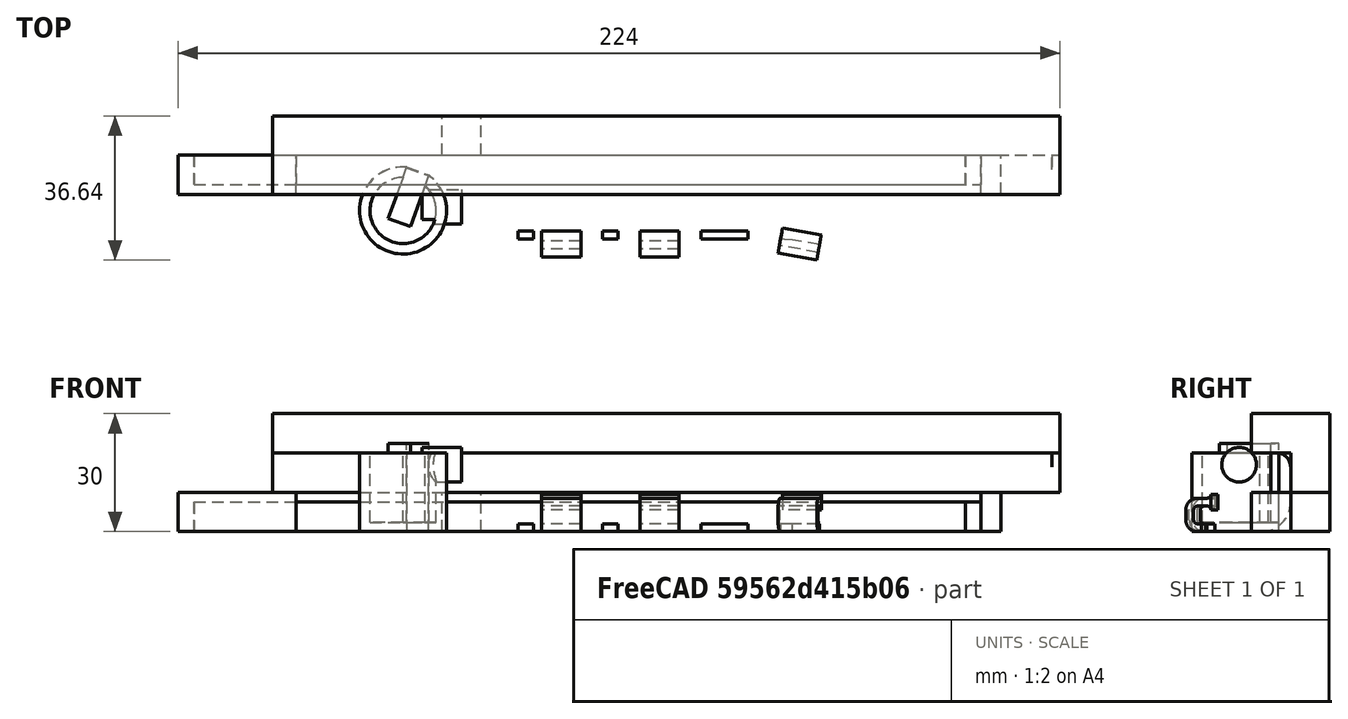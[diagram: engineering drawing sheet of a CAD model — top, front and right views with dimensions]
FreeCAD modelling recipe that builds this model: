
FCSTD DOCUMENT  (FreeCAD 0.19R0.19.2)
Label: v0_71
License: All rights reserved
LicenseURL: http://en.wikipedia.org/wiki/All_rights_reserved
objects: Part::Box×62, Part::Fillet×31, Part::MultiFuse×26, Part::Cut×14, Sketcher::SketchObject×10, Part::Extrusion×9, Part::Cylinder×6, App::MeasureDistance×3, Part::Revolution×1
note: 159 computed .brp shape members not serialized (recipe doc carries the construction recipe); baked Part::Feature solids carry a one-line shape summary decoded from their .brp

FEATURE [Sketcher::SketchObject] Sketch001
  FullyConstrained = true
  sketch-geometry (47):
    g0: Circle CenterX=-129.5 CenterY=-8 CenterZ=0 NormalX=0 NormalY=0 NormalZ=1 AngleXU=0 Radius=1
    g1: Circle CenterX=-129.5 CenterY=-3 CenterZ=0 NormalX=0 NormalY=0 NormalZ=1 AngleXU=0 Radius=1
    g2: Circle CenterX=-124.5 CenterY=-3 CenterZ=0 NormalX=0 NormalY=0 NormalZ=1 AngleXU=0 Radius=1
    g3: BSplineCurve PolesCount=3 KnotsCount=2 Degree=2 IsPeriodic=0
    g4: GeomPoint X=-129.5 Y=-8 Z=0
    g5: GeomPoint X=-124.5 Y=-3 Z=0
    g6: LineSegment StartX=18.6 StartY=-2.9 StartZ=0 EndX=23.6 EndY=-2.9 EndZ=0
    g7: ArcOfCircle CenterX=23.8 CenterY=-14.35 CenterZ=0 NormalX=0 NormalY=0 NormalZ=1 AngleXU=0 Radius=2.3 StartAngle=8e-16 EndAngle=1.5708
    g8: ArcOfCircle CenterX=23.8 CenterY=-18.1 CenterZ=0 NormalX=0 NormalY=0 NormalZ=1 AngleXU=0 Radius=2.3 StartAngle=4.71239 EndAngle=6.28319
    g9: LineSegment StartX=23.8 StartY=-20.4 StartZ=0 EndX=21.1 EndY=-20.4 EndZ=0
    g10: LineSegment StartX=21.1 StartY=-22.9 StartZ=0 EndX=21.1 EndY=-20.4 EndZ=0
    g11: LineSegment StartX=26.1 StartY=-14.35 StartZ=0 EndX=26.1 EndY=-18.1 EndZ=0
    g12: LineSegment StartX=18.6 StartY=-5.40742 StartZ=0 EndX=18.6 EndY=-2.9 EndZ=0
    g13: ArcOfCircle CenterX=18.8 CenterY=-8.1 CenterZ=0 NormalX=0 NormalY=0 NormalZ=1 AngleXU=0 Radius=2.7 StartAngle=1.64494 EndAngle=3.14159
    g14: ArcOfCircle CenterX=18.8 CenterY=-11.85 CenterZ=0 NormalX=0 NormalY=0 NormalZ=1 AngleXU=0 Radius=2.7 StartAngle=3.14159 EndAngle=4.71239
    g15: LineSegment StartX=16.1 StartY=-8.1 StartZ=0 EndX=16.1 EndY=-11.85 EndZ=0
    g16: LineSegment StartX=18.8 StartY=-14.55 StartZ=0 EndX=21.5 EndY=-14.55 EndZ=0
    g17: LineSegment StartX=21.5 StartY=-12.05 StartZ=0 EndX=21.5 EndY=-14.55 EndZ=0
    g18: LineSegment StartX=21.5 StartY=-12.05 StartZ=0 EndX=23.8 EndY=-12.05 EndZ=0
    g19: LineSegment StartX=16.1 StartY=-22.9 StartZ=0 EndX=21.1 EndY=-22.9 EndZ=0
    g20: LineSegment StartX=23.6 StartY=-2.9 StartZ=0 EndX=23.6 EndY=0 EndZ=0
    g21: LineSegment StartX=16.1 StartY=-22.9 StartZ=0 EndX=16.1 EndY=-26.2 EndZ=0
    g22: BSplineCurve PolesCount=3 KnotsCount=2 Degree=2 IsPeriodic=0
    g23: LineSegment StartX=2.6 StartY=-3 StartZ=0 EndX=-124.5 EndY=-3 EndZ=0
    g24: ArcOfCircle CenterX=-134.9 CenterY=-8.6 CenterZ=0 NormalX=0 NormalY=0 NormalZ=1 AngleXU=0 Radius=0.5 StartAngle=4.71238 EndAngle=6.28319
    g25: LineSegment StartX=-141.9 StartY=-9.1 StartZ=0 EndX=-134.9 EndY=-9.1 EndZ=0
    g26: LineSegment StartX=-141.9 StartY=-33.8 StartZ=0 EndX=-141.5 EndY=-33.8 EndZ=0
    g27: LineSegment StartX=-141.9 StartY=-9.1 StartZ=0 EndX=-141.9 EndY=-33.8 EndZ=0
    g28: LineSegment StartX=-134.4 StartY=-8.6 StartZ=0 EndX=-134.4 EndY=0 EndZ=0
    g29: LineSegment StartX=-134.4 StartY=0 StartZ=0 EndX=23.6 EndY=0 EndZ=0
    g30: LineSegment StartX=-133.5 StartY=-26.2 StartZ=0 EndX=16.1 EndY=-26.2 EndZ=0
    g31-g36: Circle x6 (B-spline internal-alignment scaffolding for g37; pole/knot coordinates omitted)
    g37: BSplineCurve PolesCount=6 KnotsCount=4 Degree=3 IsPeriodic=0
    g38-g41: GeomPoint x4 (B-spline internal-alignment scaffolding for g37; pole/knot coordinates omitted)
    g42: BSplineCurve PolesCount=3 KnotsCount=2 Degree=2 IsPeriodic=0
    g43: LineSegment StartX=-129.5 StartY=-8 StartZ=0 EndX=-129.5 EndY=-18.2 EndZ=0
    g44: BSplineCurve PolesCount=3 KnotsCount=2 Degree=2 IsPeriodic=0
    g45: LineSegment StartX=7.6 StartY=-8 StartZ=0 EndX=7.6 EndY=-18.2 EndZ=0
    g46: LineSegment StartX=2.6 StartY=-23.2 StartZ=0 EndX=-124.5 EndY=-23.2 EndZ=0
  constraints (87):
    c: Weight(g0) = 1
    c: Equal(g0,g1)
    c: Equal(g0,g2)
    c: InternalAlignment(g0,g3)
    c: InternalAlignment(g1,g3)
    c: InternalAlignment(g2,g3)
    c: InternalAlignment(g4,g3)
    c: InternalAlignment(g5,g3)
    c: Block(g3)
    c: Block(g8)
    c: Block(g7)
    c: Coincident(g9,g8)
    c: Horizontal(g9)
    c: Vertical(g10)
    c: Coincident(g10,g9)
    c: Coincident(g11,g7)
    c: Coincident(g11,g8)
    c: Vertical(g11)
    c: Vertical(g12)
    c: Block(g12)
    c: Coincident(g6,g12)
    c: Horizontal(g6)
    c: Block(g6)
    c: Coincident(g13,g12)
    c: Block(g14)
    c: Vertical(g15)
    c: Block(g15)
    c: Coincident(g16,g14)
    c: Horizontal(g16)
    c: Vertical(g17)
    c: Coincident(g17,g16)
    c: Block(g17)
    c: Coincident(g18,g7)
    c: Horizontal(g18)
    c: Block(g18)
    c: Coincident(g19,g10)
    c: Horizontal(g19)
    c: Block(g19)
    c: Block(g13)
    c: Coincident(g20,g6)
    c: Vertical(g20)
    c: Vertical(g21)
    c: Block(g21)
    c: Block(g22)
    c: Coincident(g23,g22)
    c: Coincident(g23,g3)
    c: Horizontal(g23)
    c: Block(g24)
    c: Coincident(g25,g24)
    c: Horizontal(g25)
    c: Horizontal(g26)
    c: Block(g26)
    c: Coincident(g27,g25)
    c: Coincident(g27,g26)
    c: Vertical(g27)
    c: Coincident(g28,g24)
    c: Vertical(g28)
    c: Coincident(g29,g28)
    c: Coincident(g29,g20)
    c: Horizontal(g29)
    c: Block(g29)
    c: Block(g25)
    c: Block(g28)
    c: Block(g27)
    c: Coincident(g30,g21)
    c: Horizontal(g30)
    c: Block(g30)
    c: Coincident(g37,g26)
    c: Weight(g31) = 1
    c: Equal(g31, g32-g36) x5
    c: Coincident(g37,g30)
    c: InternalAlignment(g31-g36 -> g37) x6
    c: InternalAlignment(g38-g41 -> g37) x4
    c: Block(g37)
    c: Block(g42)
    c: Coincident(g43,g3)
    c: Coincident(g43,g42)
    c: Vertical(g43)
    c: Distance(g43) = 10.2
    c: Block(g44)
    c: Coincident(g45,g22)
    c: Coincident(g45,g44)
    c: Vertical(g45)
    c: Distance(g45) = 10.2
    c: Coincident(g46,g44)
    c: Coincident(g46,g42)
    c: Horizontal(g46)
FEATURE [Part::Extrusion] Extrude001
  Base = -> Sketch001
  Dir = (0,0,1)
  DirMode = 2
  FaceMakerClass = Part::FaceMakerBullseye
  LengthFwd = 20
  LengthRev = 0
  Solid = true
  Symmetric = false
FEATURE [Sketcher::SketchObject] Sketch004
  FullyConstrained = true
  Placement = pos=(0,0,0) rot=(1,0,0;1.5708rad)
  sketch-geometry (12):
    g0: LineSegment StartX=15.75 StartY=2.5 StartZ=0 EndX=15.75 EndY=0 EndZ=0
    g1: Circle CenterX=15.75 CenterY=2.5 CenterZ=0 NormalX=0 NormalY=0 NormalZ=1 AngleXU=0 Radius=1
    g2: Circle CenterX=10.55 CenterY=2.5 CenterZ=0 NormalX=0 NormalY=0 NormalZ=1 AngleXU=0 Radius=1
    g3: Circle CenterX=10.55 CenterY=8 CenterZ=0 NormalX=0 NormalY=0 NormalZ=1 AngleXU=0 Radius=1
    g4: BSplineCurve PolesCount=3 KnotsCount=2 Degree=2 IsPeriodic=0
    g5: GeomPoint X=15.75 Y=2.5 Z=0
    g6: GeomPoint X=10.55 Y=8 Z=0
    g7: LineSegment StartX=1.9 StartY=8 StartZ=0 EndX=10.55 EndY=8 EndZ=0
    g8: LineSegment StartX=1.9 StartY=-2.4 StartZ=0 EndX=1.9 EndY=8 EndZ=0
    g9: LineSegment StartX=3.30092 StartY=-2.4 StartZ=0 EndX=3.30092 EndY=0 EndZ=0
    g10: LineSegment StartX=15.75 StartY=0 StartZ=0 EndX=3.30092 EndY=0 EndZ=0
    g11: LineSegment StartX=3.30092 StartY=-2.4 StartZ=0 EndX=1.9 EndY=-2.4 EndZ=0
  constraints (26):
    c: Vertical(g0)
    c: Distance(g0) = 2.5
    c: Coincident(g4,g0)
    c: Weight(g1) = 1
    c: Equal(g1,g2)
    c: Equal(g1,g3)
    c: InternalAlignment(g1,g4)
    c: InternalAlignment(g2,g4)
    c: InternalAlignment(g3,g4)
    c: InternalAlignment(g5,g4)
    c: InternalAlignment(g6,g4)
    c: Block(g4)
    c: Coincident(g7,g4)
    c: Horizontal(g7)
    c: Vertical(g8)
    c: Coincident(g8,g7)
    c: Block(g8)
    c: Vertical(g9)
    c: Coincident(g10,g0)
    c: PointOnObject(g10,g-1)
    c: Horizontal(g10)
    c: Coincident(g10,g9)
    c: Block(g9)
    c: Coincident(g11,g9)
    c: Coincident(g11,g8)
    c: Horizontal(g11)
FEATURE [Part::Revolution] Revolve  label="mainScrewStandRevolve"
  Angle = 360
  Axis = (0,0,1)
  Base = (0,0,0)
  FaceMakerClass = Part::FaceMakerBullseye
  Placement = pos=(-101.95,-15.3,0) rot=(0,0,1;0rad)
  Solid = true
  Source = -> Sketch004
  Symmetric = false
FEATURE [Sketcher::SketchObject] Sketch044
  FullyConstrained = true
  MapMode = 4
  Placement = pos=(0,0,0) rot=(0.57735,0.57735,0.57735;2.0944rad)
  sketch-geometry (14):
    g0: LineSegment StartX=6.08745 StartY=-4.11588 StartZ=0 EndX=6.08745 EndY=-2.11589 EndZ=0
    g1: LineSegment StartX=8.08745 StartY=1.38411 StartZ=0 EndX=8.08745 EndY=-1.11589 EndZ=0
    g2: ArcOfCircle CenterX=7.08745 CenterY=-1.11589 CenterZ=0 NormalX=0 NormalY=0 NormalZ=1 AngleXU=0 Radius=1 StartAngle=4.71239 EndAngle=6.28319
    g3: LineSegment StartX=6.08745 StartY=-2.11589 StartZ=0 EndX=7.08745 EndY=-2.11589 EndZ=0
    g4: LineSegment StartX=6.08745 StartY=-4.11588 StartZ=0 EndX=7.08745 EndY=-4.11588 EndZ=0
    g5: ArcOfCircle CenterX=7.08745 CenterY=-1.11589 CenterZ=0 NormalX=0 NormalY=0 NormalZ=1 AngleXU=0 Radius=3 StartAngle=4.71239 EndAngle=6.28319
    g6: ArcOfCircle CenterX=7.08745 CenterY=1.38411 CenterZ=0 NormalX=0 NormalY=0 NormalZ=1 AngleXU=0 Radius=1 StartAngle=5.35e-14 EndAngle=1.5708
    g7: LineSegment StartX=10.0875 StartY=-1.11588 StartZ=0 EndX=10.0875 EndY=1.38411 EndZ=0
    g8: ArcOfCircle CenterX=7.08745 CenterY=1.38411 CenterZ=0 NormalX=0 NormalY=0 NormalZ=1 AngleXU=0 Radius=3 StartAngle=3.57e-14 EndAngle=1.5708
    g9: ArcOfCircle CenterX=4.58745 CenterY=1.38412 CenterZ=0 NormalX=0 NormalY=0 NormalZ=1 AngleXU=0 Radius=1 StartAngle=1.57081 EndAngle=3.14159
    g10: LineSegment StartX=4.58744 StartY=2.38411 StartZ=0 EndX=7.08745 EndY=2.38411 EndZ=0
    g11: LineSegment StartX=4.58745 StartY=4.38411 StartZ=0 EndX=7.08745 EndY=4.38411 EndZ=0
    g12: ArcOfCircle CenterX=4.58745 CenterY=5.38411 CenterZ=0 NormalX=0 NormalY=0 NormalZ=1 AngleXU=0 Radius=1 StartAngle=3.14159 EndAngle=4.71239
    g13: LineSegment StartX=3.58745 StartY=5.38411 StartZ=0 EndX=3.58745 EndY=1.38411 EndZ=0
  constraints (33):
    c: Vertical(g0)
    c: Block(g0)
    c: Block(g1)
    c: Coincident(g2,g1)
    c: Coincident(g3,g0)
    c: Coincident(g3,g2)
    c: Horizontal(g3)
    c: Block(g2)
    c: Coincident(g4,g0)
    c: Horizontal(g4)
    c: Coincident(g5,g2)
    c: Block(g5)
    c: Block(g4)
    c: Coincident(g6,g1)
    c: Block(g6)
    c: Coincident(g7,g5)
    c: Vertical(g7)
    c: Coincident(g8,g6)
    c: Block(g8)
    c: Block(g7)
    c: Coincident(g10,g9)
    c: Coincident(g10,g6)
    c: Horizontal(g10)
    c: Block(g10)
    c: Block(g9)
    c: Coincident(g11,g8)
    c: Horizontal(g11)
    c: Block(g12)
    c: Block(g11)
    c: Coincident(g13,g12)
    c: Coincident(g13,g9)
    c: Vertical(g13)
    c: Tangent(g13,g9)
FEATURE [Part::Extrusion] Extrude039
  Base = -> Sketch044
  Dir = (1,0,0)
  DirMode = 2
  FaceMakerClass = Part::FaceMakerBullseye
  LengthFwd = 10
  LengthRev = 0
  Placement = pos=(-46.7,-15.71,4.115) rot=(0,0,1;3.14159rad)
  Solid = true
  Symmetric = false
FEATURE [Sketcher::SketchObject] Sketch045
  FullyConstrained = true
  MapMode = 4
  Placement = pos=(0,0,0) rot=(0.57735,0.57735,0.57735;2.0944rad)
  sketch-geometry (14):
    g0: LineSegment StartX=6.08745 StartY=-4.11588 StartZ=0 EndX=6.08745 EndY=-2.11589 EndZ=0
    g1: LineSegment StartX=8.08745 StartY=1.38411 StartZ=0 EndX=8.08745 EndY=-1.11589 EndZ=0
    g2: ArcOfCircle CenterX=7.08745 CenterY=-1.11589 CenterZ=0 NormalX=0 NormalY=0 NormalZ=1 AngleXU=0 Radius=1 StartAngle=4.71239 EndAngle=6.28319
    g3: LineSegment StartX=6.08745 StartY=-2.11589 StartZ=0 EndX=7.08745 EndY=-2.11589 EndZ=0
    g4: LineSegment StartX=6.08745 StartY=-4.11588 StartZ=0 EndX=7.08745 EndY=-4.11588 EndZ=0
    g5: ArcOfCircle CenterX=7.08745 CenterY=-1.11589 CenterZ=0 NormalX=0 NormalY=0 NormalZ=1 AngleXU=0 Radius=3 StartAngle=4.71239 EndAngle=6.28319
    g6: ArcOfCircle CenterX=7.08745 CenterY=1.38411 CenterZ=0 NormalX=0 NormalY=0 NormalZ=1 AngleXU=0 Radius=1 StartAngle=5.35e-14 EndAngle=1.5708
    g7: LineSegment StartX=10.0875 StartY=-1.11588 StartZ=0 EndX=10.0875 EndY=1.38411 EndZ=0
    g8: ArcOfCircle CenterX=7.08745 CenterY=1.38411 CenterZ=0 NormalX=0 NormalY=0 NormalZ=1 AngleXU=0 Radius=3 StartAngle=3.57e-14 EndAngle=1.5708
    g9: ArcOfCircle CenterX=4.58745 CenterY=1.38412 CenterZ=0 NormalX=0 NormalY=0 NormalZ=1 AngleXU=0 Radius=1 StartAngle=1.57081 EndAngle=3.14159
    g10: LineSegment StartX=4.58744 StartY=2.38411 StartZ=0 EndX=7.08745 EndY=2.38411 EndZ=0
    g11: LineSegment StartX=4.58745 StartY=4.38411 StartZ=0 EndX=7.08745 EndY=4.38411 EndZ=0
    g12: ArcOfCircle CenterX=4.58745 CenterY=5.38411 CenterZ=0 NormalX=0 NormalY=0 NormalZ=1 AngleXU=0 Radius=1 StartAngle=3.14159 EndAngle=4.71239
    g13: LineSegment StartX=3.58745 StartY=5.38411 StartZ=0 EndX=3.58745 EndY=1.38411 EndZ=0
  constraints (33):
    c: Vertical(g0)
    c: Block(g0)
    c: Block(g1)
    c: Coincident(g2,g1)
    c: Coincident(g3,g0)
    c: Coincident(g3,g2)
    c: Horizontal(g3)
    c: Block(g2)
    c: Coincident(g4,g0)
    c: Horizontal(g4)
    c: Coincident(g5,g2)
    c: Block(g5)
    c: Block(g4)
    c: Coincident(g6,g1)
    c: Block(g6)
    c: Coincident(g7,g5)
    c: Vertical(g7)
    c: Coincident(g8,g6)
    c: Block(g8)
    c: Block(g7)
    c: Coincident(g10,g9)
    c: Coincident(g10,g6)
    c: Horizontal(g10)
    c: Block(g10)
    c: Block(g9)
    c: Coincident(g11,g8)
    c: Horizontal(g11)
    c: Block(g12)
    c: Block(g11)
    c: Coincident(g13,g12)
    c: Coincident(g13,g9)
    c: Vertical(g13)
    c: Tangent(g13,g9)
FEATURE [Part::Extrusion] Extrude040
  Base = -> Sketch045
  Dir = (1,0,0)
  DirMode = 2
  FaceMakerClass = Part::FaceMakerBullseye
  LengthFwd = 10
  LengthRev = 0
  Placement = pos=(-71.7,-15.71,4.115) rot=(0,0,1;3.14159rad)
  Solid = true
  Symmetric = false
FEATURE [Part::Box] Box017  label="Cube017"
  AttacherType = Attacher::AttachEngine3D
  Height = 2
  Length = 2
  Placement = pos=(-85.7,-21.3,0) rot=(0,0,1;0rad)
  Width = 2
FEATURE [Part::Box] Box018  label="Cube018"
  AttacherType = Attacher::AttachEngine3D
  Height = 2
  Length = 2
  Placement = pos=(-87.7,-21.3,0) rot=(0,0,1;0rad)
  Width = 2
FEATURE [Part::MultiFuse] Fusion
  Shapes = -> [Box017,Box018]
FEATURE [Part::Box] Box021  label="Cube021"
  AttacherType = Attacher::AttachEngine3D
  Height = 2
  Length = 2
  Placement = pos=(-85.7,-21.3,0) rot=(0,0,1;0rad)
  Width = 2
FEATURE [Part::Box] Box022  label="Cube022"
  AttacherType = Attacher::AttachEngine3D
  Height = 2
  Length = 2
  Placement = pos=(-87.7,-21.3,0) rot=(0,0,1;0rad)
  Width = 2
FEATURE [Part::Box] Box023  label="Cube023"
  AttacherType = Attacher::AttachEngine3D
  Height = 2
  Length = 2
  Placement = pos=(-85.7,-21.3,0) rot=(0,0,1;0rad)
  Width = 2
FEATURE [Part::Box] Box024  label="Cube024"
  AttacherType = Attacher::AttachEngine3D
  Height = 2
  Length = 2
  Placement = pos=(-87.7,-21.3,0) rot=(0,0,1;0rad)
  Width = 2
FEATURE [Part::Box] Box026  label="Cube026"
  AttacherType = Attacher::AttachEngine3D
  Height = 2
  Length = 2
  Placement = pos=(-87.7,-21.3,0) rot=(0,0,1;0rad)
  Width = 2
FEATURE [Part::Box] Box  label="Cube"
  AttacherType = Attacher::AttachEngine3D
  Height = 10
  Length = 10
  Placement = pos=(-107,0,0) rot=(0,0,1;0rad)
  Width = 10
FEATURE [Sketcher::SketchObject] Sketch046
  FullyConstrained = true
  MapMode = 4
  Placement = pos=(0,0,0) rot=(0.57735,0.57735,0.57735;2.0944rad)
  sketch-geometry (14):
    g0: LineSegment StartX=6.08745 StartY=-4.11588 StartZ=0 EndX=6.08745 EndY=-2.11589 EndZ=0
    g1: LineSegment StartX=8.08745 StartY=1.38411 StartZ=0 EndX=8.08745 EndY=-1.11589 EndZ=0
    g2: ArcOfCircle CenterX=7.08745 CenterY=-1.11589 CenterZ=0 NormalX=0 NormalY=0 NormalZ=1 AngleXU=0 Radius=1 StartAngle=4.71239 EndAngle=6.28319
    g3: LineSegment StartX=6.08745 StartY=-2.11589 StartZ=0 EndX=7.08745 EndY=-2.11589 EndZ=0
    g4: LineSegment StartX=6.08745 StartY=-4.11588 StartZ=0 EndX=7.08745 EndY=-4.11588 EndZ=0
    g5: ArcOfCircle CenterX=7.08745 CenterY=-1.11589 CenterZ=0 NormalX=0 NormalY=0 NormalZ=1 AngleXU=0 Radius=3 StartAngle=4.71239 EndAngle=6.28319
    g6: ArcOfCircle CenterX=7.08745 CenterY=1.38411 CenterZ=0 NormalX=0 NormalY=0 NormalZ=1 AngleXU=0 Radius=1 StartAngle=5.35e-14 EndAngle=1.5708
    g7: LineSegment StartX=10.0875 StartY=-1.11588 StartZ=0 EndX=10.0875 EndY=1.38411 EndZ=0
    g8: ArcOfCircle CenterX=7.08745 CenterY=1.38411 CenterZ=0 NormalX=0 NormalY=0 NormalZ=1 AngleXU=0 Radius=3 StartAngle=3.57e-14 EndAngle=1.5708
    g9: ArcOfCircle CenterX=4.58745 CenterY=1.38412 CenterZ=0 NormalX=0 NormalY=0 NormalZ=1 AngleXU=0 Radius=1 StartAngle=1.57081 EndAngle=3.14159
    g10: LineSegment StartX=4.58744 StartY=2.38411 StartZ=0 EndX=7.08745 EndY=2.38411 EndZ=0
    g11: LineSegment StartX=4.58745 StartY=4.38411 StartZ=0 EndX=7.08745 EndY=4.38411 EndZ=0
    g12: ArcOfCircle CenterX=4.58745 CenterY=5.38411 CenterZ=0 NormalX=0 NormalY=0 NormalZ=1 AngleXU=0 Radius=1 StartAngle=3.14159 EndAngle=4.71239
    g13: LineSegment StartX=3.58745 StartY=5.38411 StartZ=0 EndX=3.58745 EndY=1.38411 EndZ=0
  constraints (33):
    c: Vertical(g0)
    c: Block(g0)
    c: Block(g1)
    c: Coincident(g2,g1)
    c: Coincident(g3,g0)
    c: Coincident(g3,g2)
    c: Horizontal(g3)
    c: Block(g2)
    c: Coincident(g4,g0)
    c: Horizontal(g4)
    c: Coincident(g5,g2)
    c: Block(g5)
    c: Block(g4)
    c: Coincident(g6,g1)
    c: Block(g6)
    c: Coincident(g7,g5)
    c: Vertical(g7)
    c: Coincident(g8,g6)
    c: Block(g8)
    c: Block(g7)
    c: Coincident(g10,g9)
    c: Coincident(g10,g6)
    c: Horizontal(g10)
    c: Block(g10)
    c: Block(g9)
    c: Coincident(g11,g8)
    c: Horizontal(g11)
    c: Block(g12)
    c: Block(g11)
    c: Coincident(g13,g12)
    c: Coincident(g13,g9)
    c: Vertical(g13)
    c: Tangent(g13,g9)
FEATURE [Part::Extrusion] Extrude041
  Base = -> Sketch046
  Dir = (1,0,0)
  DirMode = 2
  FaceMakerClass = Part::FaceMakerBullseye
  LengthFwd = 10
  LengthRev = 0
  Placement = pos=(-10,-16.71,4.115) rot=(0,0,1;2.96706rad)
  Solid = true
  Symmetric = false
FEATURE [Part::Box] Box027  label="Cube027"
  AttacherType = Attacher::AttachEngine3D
  Height = 2
  Length = 2
  Placement = pos=(-85.7,-21.3,0) rot=(0,0,1;0rad)
  Width = 2
FEATURE [Part::Box] Box028  label="Cube028"
  AttacherType = Attacher::AttachEngine3D
  Height = 2
  Length = 2
  Placement = pos=(-87.7,-21.3,0) rot=(0,0,1;0rad)
  Width = 2
FEATURE [Part::MultiFuse] Fusion009
  Placement = pos=(21.5,0,0) rot=(0,0,1;0rad)
  Shapes = -> [Box027,Box028]
FEATURE [Part::Box] Box029  label="Cube029"
  AttacherType = Attacher::AttachEngine3D
  Height = 2
  Length = 2
  Placement = pos=(-87.7,-21.3,0) rot=(0,0,1;0rad)
  Width = 2
FEATURE [Part::Box] Box030  label="Cube030"
  AttacherType = Attacher::AttachEngine3D
  Height = 2
  Length = 2
  Placement = pos=(-85.7,-21.3,0) rot=(0,0,1;0rad)
  Width = 2
FEATURE [Part::MultiFuse] Fusion010
  Shapes = -> [Box030,Box029]
FEATURE [Part::Box] Box032  label="Cube032"
  AttacherType = Attacher::AttachEngine3D
  Height = 2
  Length = 2
  Placement = pos=(-85.7,-21.3,0) rot=(0,0,1;0rad)
  Width = 2
FEATURE [Part::Box] Box033  label="Cube033"
  AttacherType = Attacher::AttachEngine3D
  Height = 2
  Length = 2
  Placement = pos=(-87.7,-21.3,0) rot=(0,0,1;0rad)
  Width = 2
FEATURE [Part::MultiFuse] Fusion011
  Shapes = -> [Box032,Box033]
FEATURE [Part::Box] Box034  label="Cube034"
  AttacherType = Attacher::AttachEngine3D
  Height = 2
  Length = 2
  Placement = pos=(-85.7,-21.3,0) rot=(0,0,1;0rad)
  Width = 2
FEATURE [Part::Box] Box035  label="Cube035"
  AttacherType = Attacher::AttachEngine3D
  Height = 2
  Length = 2
  Placement = pos=(-87.7,-21.3,0) rot=(0,0,1;0rad)
  Width = 2
FEATURE [Part::Box] Box036  label="Cube036"
  AttacherType = Attacher::AttachEngine3D
  Height = 2
  Length = 2
  Placement = pos=(-85.7,-21.3,0) rot=(0,0,1;0rad)
  Width = 2
FEATURE [Part::Box] Box037  label="Cube037"
  AttacherType = Attacher::AttachEngine3D
  Height = 2
  Length = 2
  Placement = pos=(-87.7,-21.3,0) rot=(0,0,1;0rad)
  Width = 2
FEATURE [Part::Box] Box038  label="Cube038"
  AttacherType = Attacher::AttachEngine3D
  Height = 2
  Length = 2
  Placement = pos=(-85.7,-21.3,0) rot=(0,0,1;0rad)
  Width = 2
FEATURE [Part::Box] Box039  label="Cube039"
  AttacherType = Attacher::AttachEngine3D
  Height = 2
  Length = 2
  Placement = pos=(-87.7,-21.3,0) rot=(0,0,1;0rad)
  Width = 2
FEATURE [Part::Box] Box040  label="Cube040"
  AttacherType = Attacher::AttachEngine3D
  Height = 2
  Length = 2
  Placement = pos=(-85.7,-21.3,0) rot=(0,0,1;0rad)
  Width = 2
FEATURE [Part::Box] Box041  label="Cube041"
  AttacherType = Attacher::AttachEngine3D
  Height = 2
  Length = 2
  Placement = pos=(-87.7,-21.3,0) rot=(0,0,1;0rad)
  Width = 2
FEATURE [Part::Box] Box042  label="Cube042"
  AttacherType = Attacher::AttachEngine3D
  Height = 2
  Length = 2
  Placement = pos=(-87.7,-21.3,0) rot=(0,0,1;0rad)
  Width = 2
FEATURE [Part::Box] Box043  label="Cube043"
  AttacherType = Attacher::AttachEngine3D
  Height = 2
  Length = 2
  Placement = pos=(-85.7,-21.3,0) rot=(0,0,1;0rad)
  Width = 2
FEATURE [Part::MultiFuse] Fusion019
  Placement = pos=(46.5,0,0) rot=(0,0,1;0rad)
  Shapes = -> [Box043,Box042]
FEATURE [Part::Box] Box044  label="Cube044"
  AttacherType = Attacher::AttachEngine3D
  Height = 2
  Length = 2
  Placement = pos=(-87.7,-21.3,0) rot=(0,0,1;0rad)
  Width = 2
FEATURE [Part::Box] Box045  label="Cube045"
  AttacherType = Attacher::AttachEngine3D
  Height = 2
  Length = 2
  Placement = pos=(-85.7,-21.3,0) rot=(0,0,1;0rad)
  Width = 2
FEATURE [Part::MultiFuse] Fusion020
  Placement = pos=(69.3,0,0) rot=(0,0,1;0rad)
  Shapes = -> [Box045,Box044]
FEATURE [Part::Box] Box046  label="Cube046"
  AttacherType = Attacher::AttachEngine3D
  Height = 2
  Length = 2
  Placement = pos=(-87.7,-21.3,0) rot=(0,0,1;0rad)
  Width = 2
FEATURE [Part::Box] Box047  label="Cube047"
  AttacherType = Attacher::AttachEngine3D
  Height = 2
  Length = 2
  Placement = pos=(-85.7,-21.3,0) rot=(0,0,1;0rad)
  Width = 2
FEATURE [Part::MultiFuse] Fusion021
  Placement = pos=(73.3,0,0) rot=(0,0,1;0rad)
  Shapes = -> [Box047,Box046]
FEATURE [Part::Box] Box048  label="Cube048"
  AttacherType = Attacher::AttachEngine3D
  Height = 2
  Length = 2
  Placement = pos=(-87.7,-21.3,0) rot=(0,0,1;0rad)
  Width = 2
FEATURE [Part::Box] Box049  label="Cube049"
  AttacherType = Attacher::AttachEngine3D
  Height = 2
  Length = 2
  Placement = pos=(-85.7,-21.3,0) rot=(0,0,1;0rad)
  Width = 2
FEATURE [Part::MultiFuse] Fusion022
  Placement = pos=(64.3,0,0) rot=(0,0,1;0rad)
  Shapes = -> [Box049,Box048]
FEATURE [Part::MultiFuse] Fusion024
  Shapes = -> [Box034,Box035,Box036,Box037,Box038,Box039,Box040,Box041]
FEATURE [Part::MultiFuse] Fusion025
  Shapes = -> [Box021,Box022,Box023,Box024,Box026]
FEATURE [Part::Box] Box005  label="Cube005"
  AttacherType = Attacher::AttachEngine3D
  Height = 10
  Length = 198
  Placement = pos=(-30,0,0) rot=(0,0,1;0rad)
  Width = 10
FEATURE [Part::Box] Box004  label="Cube004"
  AttacherType = Attacher::AttachEngine3D
  Height = 10
  Length = 200
  Placement = pos=(-30,0,0) rot=(0,0,1;0rad)
  Width = 10
FEATURE [Part::Fillet] Fillet020
  Base = -> Box004
  Edges = 1 edges r=3.6: [Edge12]
FEATURE [Sketcher::SketchObject] Sketch
  FullyConstrained = true
  sketch-geometry (35):
    g0: Circle CenterX=-101.95 CenterY=-14.3 CenterZ=0 NormalX=0 NormalY=0 NormalZ=1 AngleXU=0 Radius=3.25
    g1: LineSegment StartX=16.1 StartY=-26.2 StartZ=0 EndX=16.1 EndY=-22.9 EndZ=0
    g2: ArcOfCircle CenterX=23.8 CenterY=-14.35 CenterZ=0 NormalX=0 NormalY=0 NormalZ=1 AngleXU=0 Radius=2.3 StartAngle=8e-16 EndAngle=1.5708
    g3: LineSegment StartX=18.6 StartY=-5.40742 StartZ=0 EndX=18.6 EndY=-2.9 EndZ=0
    g4: LineSegment StartX=18.6 StartY=-2.9 StartZ=0 EndX=23.6 EndY=-2.9 EndZ=0
    g5: LineSegment StartX=23.6 StartY=-2.9 StartZ=0 EndX=23.6 EndY=2.58e-14 EndZ=0
    g6: LineSegment StartX=18.8 StartY=-14.55 StartZ=0 EndX=21.5 EndY=-14.55 EndZ=0
    g7: LineSegment StartX=21.5 StartY=-12.05 StartZ=0 EndX=21.5 EndY=-14.55 EndZ=0
    g8: LineSegment StartX=21.5 StartY=-12.05 StartZ=0 EndX=23.8 EndY=-12.05 EndZ=0
    g9: ArcOfCircle CenterX=23.8 CenterY=-18.1 CenterZ=0 NormalX=0 NormalY=0 NormalZ=1 AngleXU=0 Radius=2.3 StartAngle=4.71239 EndAngle=6.28319
    g10: LineSegment StartX=23.8 StartY=-20.4 StartZ=0 EndX=21.1 EndY=-20.4 EndZ=0
    g11: LineSegment StartX=26.1 StartY=-14.35 StartZ=0 EndX=26.1 EndY=-18.1 EndZ=0
    g12: ArcOfCircle CenterX=18.8 CenterY=-8.1 CenterZ=0 NormalX=0 NormalY=0 NormalZ=1 AngleXU=0 Radius=2.7 StartAngle=1.64494 EndAngle=3.14159
    g13: ArcOfCircle CenterX=18.8 CenterY=-11.85 CenterZ=0 NormalX=0 NormalY=0 NormalZ=1 AngleXU=0 Radius=2.7 StartAngle=3.14159 EndAngle=4.71239
    g14: LineSegment StartX=16.1 StartY=-8.1 StartZ=0 EndX=16.1 EndY=-11.85 EndZ=0
    g15: LineSegment StartX=21.1 StartY=-22.9 StartZ=0 EndX=21.1 EndY=-20.4 EndZ=0
    g16: LineSegment StartX=16.1 StartY=-22.9 StartZ=0 EndX=21.1 EndY=-22.9 EndZ=0
    g17: LineSegment StartX=23.6 StartY=2.58e-14 StartZ=0 EndX=-134.4 EndY=2.58e-14 EndZ=0
    g18: LineSegment StartX=-134.4 StartY=2.59e-14 StartZ=0 EndX=-134.4 EndY=-8.6 EndZ=0
    g19: ArcOfCircle CenterX=-134.9 CenterY=-8.6 CenterZ=0 NormalX=0 NormalY=0 NormalZ=1 AngleXU=0 Radius=0.5 StartAngle=4.71238 EndAngle=6.28319
    g20: LineSegment StartX=-134.9 StartY=-9.1 StartZ=0 EndX=-141.9 EndY=-9.1 EndZ=0
    g21: LineSegment StartX=-141.9 StartY=-9.1 StartZ=0 EndX=-141.9 EndY=-33.8 EndZ=0
    g22: LineSegment StartX=-141.9 StartY=-33.8 StartZ=0 EndX=-141.5 EndY=-33.8 EndZ=0
    g23: LineSegment StartX=-133.5 StartY=-26.2 StartZ=0 EndX=16.1 EndY=-26.2 EndZ=0
    g24-g29: Circle x6 (B-spline internal-alignment scaffolding for g30; pole/knot coordinates omitted)
    g30: BSplineCurve PolesCount=6 KnotsCount=4 Degree=3 IsPeriodic=0
    g31-g34: GeomPoint x4 (B-spline internal-alignment scaffolding for g30; pole/knot coordinates omitted)
  constraints (61):
    c: Block(g0)
    c: Vertical(g1)
    c: Distance(g1) = 3.3
    c: Block(g9)
    c: Block(g2)
    c: Coincident(g10,g9)
    c: Horizontal(g10)
    c: Vertical(g15)
    c: Coincident(g15,g10)
    c: Coincident(g11,g2)
    c: Coincident(g11,g9)
    c: Vertical(g11)
    c: Vertical(g3)
    c: Block(g3)
    c: Coincident(g4,g3)
    c: Horizontal(g4)
    c: Vertical(g5)
    c: Block(g5)
    c: Block(g4)
    c: Coincident(g12,g3)
    c: Block(g13)
    c: Coincident(g14,g12)
    c: Vertical(g14)
    c: Block(g14)
    c: Coincident(g6,g13)
    c: Horizontal(g6)
    c: Vertical(g7)
    c: Coincident(g7,g6)
    c: Block(g7)
    c: Coincident(g8,g2)
    c: Horizontal(g8)
    c: Block(g8)
    c: Coincident(g16,g15)
    c: Horizontal(g16)
    c: Block(g16)
    c: Block(g12)
    c: Coincident(g16,g1)
    c: Coincident(g17,g5)
    c: Horizontal(g17)
    c: Vertical(g18)
    c: Horizontal(g20)
    c: Coincident(g19,g18)
    c: Coincident(g19,g20)
    c: Block(g19)
    c: Coincident(g21,g20)
    c: Vertical(g21)
    c: Block(g21)
    c: Coincident(g22,g21)
    c: Horizontal(g22)
    c: Block(g22)
    c: Block(g18)
    c: Coincident(g18,g17)
    c: Coincident(g23,g1)
    c: Horizontal(g23)
    c: Distance(g23) = 149.6
    c: Coincident(g30,g22)
    c: Weight(g24) = 1
    c: Equal(g24, g25-g29) x5
    c: InternalAlignment(g24-g29 -> g30) x6
    c: InternalAlignment(g31-g34 -> g30) x4
    c: Block(g30)
FEATURE [Part::Extrusion] Extrude
  Base = -> Sketch
  Dir = (0,0,1)
  DirMode = 2
  FaceMakerClass = Part::FaceMakerBullseye
  LengthFwd = 2.4
  LengthRev = 0
  Solid = true
  Symmetric = false
FEATURE [Part::Box] Box051  label="Cube051"
  AttacherType = Attacher::AttachEngine3D
  Height = 10
  Length = 198
  Placement = pos=(-30,0,0) rot=(0,0,1;0rad)
  Width = 10
FEATURE [Part::Box] Box052  label="Cube052"
  AttacherType = Attacher::AttachEngine3D
  Height = 5
  Length = 200
  Placement = pos=(-30,6.4,10) rot=(1,0,0;0rad)
  Width = 5
FEATURE [Part::Box] Box053  label="Cube053"
  AttacherType = Attacher::AttachEngine3D
  Height = 5
  Length = 200
  Placement = pos=(-30,6.4,10) rot=(1,0,0;0.872665rad)
  Width = 5
FEATURE [Part::Box] Box054  label="Cube054"
  AttacherType = Attacher::AttachEngine3D
  Height = 10
  Length = 200
  Placement = pos=(-30,0,0) rot=(0,0,1;0rad)
  Width = 10
FEATURE [Part::Fillet] Fillet021
  Base = -> Box054
  Edges = 1 edges r=3.6: [Edge12]
FEATURE [Part::Cut] Cut015
  Base = -> Box051
  Tool = -> Fillet021
FEATURE [Part::MultiFuse] Fusion033  label="removeFromMainFusion014"
  Placement = pos=(-120,-10,10) rot=(0,0,1;0rad)
  Shapes = -> [Box053,Box052,Cut015]
FEATURE [Part::Box] Box055  label="Cube055"
  AttacherType = Attacher::AttachEngine3D
  Height = 10
  Length = 190
  Placement = pos=(-30,0,0) rot=(0,0,1;0rad)
  Width = 10
FEATURE [Part::Box] Box056  label="Cube056"
  AttacherType = Attacher::AttachEngine3D
  Height = 10
  Length = 190
  Placement = pos=(-35,0,0) rot=(0,0,1;0rad)
  Width = 10
FEATURE [Part::Fillet] Fillet022
  Base = -> Box055
  Edges = 1 edges r=7.5: [Edge11]
FEATURE [Part::Cut] Cut014  label="filletMain001"
  Base = -> Box056
  Placement = pos=(-120,-10,0) rot=(0,0,1;0rad)
  Tool = -> Fillet022
FEATURE [Part::MultiFuse] Fusion032  label="removeFromMain001"
  Shapes = -> [Fusion033,Cut014]
FEATURE [Part::Cut] Cut017
  Base = -> Extrude
  Tool = -> Fusion032
FEATURE [Part::Box] Box063  label="Cube063"
  AttacherType = Attacher::AttachEngine3D
  Height = 10
  Length = 198
  Placement = pos=(-30,0,0) rot=(0,0,1;0rad)
  Width = 10
FEATURE [Part::Box] Box064  label="Cube064"
  AttacherType = Attacher::AttachEngine3D
  Height = 5
  Length = 200
  Placement = pos=(-30,6.4,10) rot=(1,0,0;0rad)
  Width = 5
FEATURE [Part::Box] Box065  label="Cube065"
  AttacherType = Attacher::AttachEngine3D
  Height = 5
  Length = 200
  Placement = pos=(-30,6.4,10) rot=(1,0,0;0.872665rad)
  Width = 5
FEATURE [Part::Box] Box066  label="Cube066"
  AttacherType = Attacher::AttachEngine3D
  Height = 10
  Length = 200
  Placement = pos=(-30,0,0) rot=(0,0,1;0rad)
  Width = 10
FEATURE [Part::Fillet] Fillet023
  Base = -> Box066
  Edges = 1 edges r=3.6: [Edge12]
FEATURE [Part::Cut] Cut018
  Base = -> Box063
  Tool = -> Fillet023
FEATURE [Part::MultiFuse] Fusion035  label="removeFromMainFusion015"
  Placement = pos=(-120,-10,10) rot=(0,0,1;0rad)
  Shapes = -> [Box065,Box064,Cut018]
FEATURE [Part::Box] Box067  label="Cube067"
  AttacherType = Attacher::AttachEngine3D
  Height = 10
  Length = 190
  Placement = pos=(-30,0,0) rot=(0,0,1;0rad)
  Width = 10
FEATURE [Part::Fillet] Fillet024
  Base = -> Box067
  Edges = 1 edges r=7.5: [Edge11]
FEATURE [Part::Box] Box068  label="Cube068"
  AttacherType = Attacher::AttachEngine3D
  Height = 10
  Length = 190
  Placement = pos=(-35,0,0) rot=(0,0,1;0rad)
  Width = 10
FEATURE [Part::Cut] Cut019  label="filletMain002"
  Base = -> Box068
  Placement = pos=(-120,-10,0) rot=(0,0,1;0rad)
  Tool = -> Fillet024
FEATURE [Part::MultiFuse] Fusion036  label="removeFromMain002"
  Shapes = -> [Fusion035,Cut019]
FEATURE [Part::Box] Box069  label="Cube069"
  AttacherType = Attacher::AttachEngine3D
  Height = 20
  Length = 10
  Placement = pos=(-144.4,-8,0) rot=(0,0,1;0rad)
  Width = 10
FEATURE [Part::Box] Box070  label="Cube070"
  AttacherType = Attacher::AttachEngine3D
  Height = 20
  Length = 30
  Placement = pos=(-120,0,0) rot=(0,0,1;0rad)
  Width = 20
FEATURE [Part::MultiFuse] Fusion037  label="removeFromIntegrityIncreaserFusion037"
  Shapes = -> [Box069,Box070,Fusion036]
FEATURE [Sketcher::SketchObject] Sketch047
  FullyConstrained = true
  sketch-geometry (4):
    g0: LineSegment StartX=20.5 StartY=-1.82002 StartZ=0 EndX=20.5 EndY=-36 EndZ=0
    g1: LineSegment StartX=32.7 StartY=-36 StartZ=0 EndX=32.7 EndY=-1.82002 EndZ=0
    g2: LineSegment StartX=20.5 StartY=-1.82002 StartZ=0 EndX=32.7 EndY=-1.82002 EndZ=0
    g3: LineSegment StartX=20.5 StartY=-36 StartZ=0 EndX=32.7 EndY=-36 EndZ=0
  constraints (12):
    c: Vertical(g0)
    c: Distance(g0) = 34.18
    c: Vertical(g1)
    c: Block(g0)
    c: Coincident(g2,g0)
    c: Horizontal(g2)
    c: Coincident(g2,g1)
    c: Block(g2)
    c: Block(g1)
    c: Coincident(g3,g0)
    c: Coincident(g3,g1)
    c: Horizontal(g3)
FEATURE [Part::MultiFuse] Fusion038
  Placement = pos=(-18.8,0,0) rot=(0,0,1;0rad)
  Shapes = -> [Fusion020,Fusion021]
FEATURE [Part::Box] Box071  label="Cube071"
  AttacherType = Attacher::AttachEngine3D
  Height = 2
  Length = 2
  Placement = pos=(-87.7,-21.3,0) rot=(0,0,1;0rad)
  Width = 2
FEATURE [Part::Box] Box072  label="Cube072"
  AttacherType = Attacher::AttachEngine3D
  Height = 2
  Length = 2
  Placement = pos=(-85.7,-21.3,0) rot=(0,0,1;0rad)
  Width = 2
FEATURE [Part::MultiFuse] Fusion039
  Placement = pos=(64.3,0,-0.5) rot=(0,0,1;0rad)
  Shapes = -> [Box072,Box071]
FEATURE [Part::MultiFuse] Fusion040  label="removeFromHook"
  Placement = pos=(2.4,-1.09,0) rot=(0,0,-1;0.045379rad)
  Shapes = -> [Fusion022,Fusion039]
FEATURE [Part::Cut] Cut
  Base = -> Extrude041
  Tool = -> Fusion040
FEATURE [Part::Cut] Cut021
  Base = -> Box005
  Tool = -> Fillet020
FEATURE [Part::Box] Box073  label="Cube073"
  AttacherType = Attacher::AttachEngine3D
  Height = 10
  Length = 200
  Placement = pos=(-30,10,0) rot=(0,0,1;0rad)
  Width = 10
FEATURE [Part::Box] Box074  label="Cube074"
  AttacherType = Attacher::AttachEngine3D
  Height = 10
  Length = 200
  Placement = pos=(-30,0,10) rot=(0,0,1;0rad)
  Width = 10
FEATURE [Part::Box] Box075  label="Cube075"
  AttacherType = Attacher::AttachEngine3D
  Height = 10
  Length = 200
  Placement = pos=(-30,10,10) rot=(0,0,1;0rad)
  Width = 10
FEATURE [Part::MultiFuse] Fusion043  label="removeFromMainFusion043"
  Placement = pos=(-120,-10,10) rot=(0,0,1;0rad)
  Shapes = -> [Cut021,Box074,Box073,Box075]
FEATURE [Part::Box] Box076  label="Cube076"
  AttacherType = Attacher::AttachEngine3D
  Height = 10
  Length = 200
  Placement = pos=(-160,0,0) rot=(0,0,1;0rad)
  Width = 10
FEATURE [Part::Box] Box077  label="Cube077"
  AttacherType = Attacher::AttachEngine3D
  Height = 10
  Length = 170
  Placement = pos=(-130,0,0) rot=(0,0,1;0rad)
  Width = 10
FEATURE [Part::Fillet] Fillet028
  Base = -> Box077
  Edges = 1 edges r=7.5: [Edge11]
FEATURE [Part::Cut] Cut024
  Base = -> Box076
  Placement = pos=(-14,-10,0) rot=(0,0,1;0rad)
  Tool = -> Fillet028
FEATURE [Part::Box] Box078  label="Cube078"
  AttacherType = Attacher::AttachEngine3D
  Height = 10
  Length = 200
  Width = 10
FEATURE [Part::Box] Box079  label="Cube079"
  AttacherType = Attacher::AttachEngine3D
  Height = 10
  Length = 205
  Placement = pos=(10,0,0) rot=(0,0,1;0rad)
  Width = 10
FEATURE [Part::Fillet] Fillet029
  Base = -> Box078
  Edges = 1 edges r=7.5: [Edge11]
  Placement = pos=(10,0,0) rot=(0,0,1;0rad)
FEATURE [Part::Cut] Cut025  label="removeFromMainCut025"
  Base = -> Box079
  Placement = pos=(-180,-10,0) rot=(0,0,1;0rad)
  Tool = -> Fillet029
FEATURE [Part::Cylinder] Cylinder001
  Angle = 360
  AttacherType = Attacher::AttachEngine3D
  Height = 10
  Placement = pos=(-36.2,-2,12) rot=(0,1,0;1.5708rad)
  Radius = 2
FEATURE [App::MeasureDistance] Distance  label="Distance: 4.02 mm"
  Distance = 4.02
  P1 = (-33.21,5.8978,9.90268)
  P2 = (-29.19,5.8978,9.90268)
FEATURE [Part::Fillet] Fillet030
  Base = -> Cylinder001
  Edges = 1 edges r=1.8: [Edge3]
FEATURE [Part::Fillet] Fillet031
  Base = -> Fillet030
  Edges = 1 edges r=1.8: [Edge2]
FEATURE [Part::Cylinder] Cylinder003
  Angle = 360
  AttacherType = Attacher::AttachEngine3D
  Height = 10
  Placement = pos=(-36.2,-2,12) rot=(0,1,0;1.5708rad)
  Radius = 2
FEATURE [Part::Fillet] Fillet035
  Base = -> Cylinder003
  Edges = 1 edges r=1.8: [Edge3]
FEATURE [Part::Fillet] Fillet036
  Base = -> Fillet035
  Edges = 1 edges r=1.8: [Edge2]
  Placement = pos=(-12.8,0,0) rot=(0,0,1;0rad)
FEATURE [Part::Cylinder] Cylinder004
  Angle = 360
  AttacherType = Attacher::AttachEngine3D
  Height = 10
  Placement = pos=(-36.2,-2,12) rot=(0,1,0;1.5708rad)
  Radius = 2
FEATURE [Part::Fillet] Fillet038
  Base = -> Cylinder004
  Edges = 1 edges r=1.8: [Edge3]
FEATURE [Part::Fillet] Fillet037
  Base = -> Fillet038
  Edges = 1 edges r=1.8: [Edge2]
  Placement = pos=(-6.4,0,0) rot=(0,0,1;0rad)
FEATURE [Sketcher::SketchObject] Sketch048
  FullyConstrained = true
  sketch-geometry (4):
    g0: LineSegment StartX=-5.1 StartY=-34.18 StartZ=0 EndX=5.1 EndY=-34.18 EndZ=0
    g1: LineSegment StartX=-5.1 StartY=-3.93167e-07 StartZ=0 EndX=-5.1 EndY=-34.18 EndZ=0
    g2: LineSegment StartX=5.1 StartY=-34.18 StartZ=0 EndX=5.1 EndY=-3.93167e-07 EndZ=0
    g3: LineSegment StartX=-5.1 StartY=-3.93167e-07 StartZ=0 EndX=5.1 EndY=-3.93167e-07 EndZ=0
  constraints (10):
    c: Horizontal(g0)
    c: Block(g0)
    c: Coincident(g1,g0)
    c: Vertical(g1)
    c: Coincident(g2,g0)
    c: Vertical(g2)
    c: Coincident(g3,g1)
    c: Coincident(g3,g2)
    c: Horizontal(g3)
    c: Block(g3)
FEATURE [Part::Extrusion] Extrude044
  Base = -> Sketch048
  Dir = (0,0,1)
  DirMode = 2
  FaceMakerClass = Part::FaceMakerBullseye
  LengthFwd = 6.2
  LengthRev = 0
  Solid = true
  Symmetric = false
FEATURE [Part::Fillet] Fillet039
  Base = -> Extrude044
  Edges = 1 edges r=3.09: [Edge7]
FEATURE [Part::Fillet] Fillet040
  Base = -> Fillet039
  Edges = 1 edges r=3.09: [Edge8]
FEATURE [Part::Fillet] Fillet041
  Base = -> Fillet040
  Edges = 1 edges r=3.09: [Edge17]
FEATURE [Part::Fillet] Fillet042  label="removeFromMainToMakeUSBCableHole"
  Base = -> Fillet041
  Edges = 1 edges r=3.09: [Edge10]
  Placement = pos=(-111.4,30,10.9) rot=(0,1,0;1.5708rad)
FEATURE [Part::Cylinder] Cylinder
  Angle = 360
  AttacherType = Attacher::AttachEngine3D
  Height = 17.6
  Placement = pos=(-116.86,-14.05,2.4) rot=(0,0,1;0rad)
  Radius = 8.4
FEATURE [Part::Box] Box080  label="Cube080"
  AttacherType = Attacher::AttachEngine3D
  Height = 20
  Length = 6
  Placement = pos=(-120.65,-16.05,2.4) rot=(0,0,-1;0.349066rad)
  Width = 13.85
FEATURE [Part::Cylinder] Cylinder005
  Angle = 360
  AttacherType = Attacher::AttachEngine3D
  Height = 20
  Placement = pos=(-116.86,-14.05,30) rot=(0,0,1;0rad)
  Radius = 11.06
FEATURE [Part::Box] Box081  label="Cube081"
  AttacherType = Attacher::AttachEngine3D
  Height = 20
  Length = 10
  Placement = pos=(-115.9,-3.3,30) rot=(0,0,-1;0.314159rad)
  Width = 10
FEATURE [App::MeasureDistance] Distance001  label="Distance: 2.40 mm"
  Distance = 2.4
  P1 = (-129.5,-19.3,2.4)
  P2 = (-129.5,-19.3,0)
FEATURE [Part::MultiFuse] Fusion047
  Shapes = -> [Box080,Cylinder]
FEATURE [Part::Cylinder] Cylinder006
  Angle = 360
  AttacherType = Attacher::AttachEngine3D
  Height = 10
  Placement = pos=(-112,-13.1,17) rot=(0,1,0;1.5708rad)
  Radius = 4.4
FEATURE [Part::MultiFuse] Fusion048  label="removeFromMainToCreateHoleForUSBCablePillar"
  Shapes = -> [Fusion047,Cylinder006]
FEATURE [Part::MultiFuse] Fusion042
  Shapes = -> [Fusion025,Fusion024,Fusion019,Fusion011,Fusion010,Fusion009,Fusion038,Extrude040,Extrude039,Fusion,Cut]
FEATURE [Part::Extrusion] Extrude046
  Base = -> Sketch047
  Dir = (0,0,1)
  DirMode = 2
  FaceMakerClass = Part::FaceMakerBullseye
  LengthFwd = 8
  LengthRev = 0
  Solid = true
  Symmetric = false
FEATURE [App::MeasureDistance] Distance002  label="Distance: 12.20 mm"
  Distance = 12.2
  P1 = (32.7,-36,8)
  P2 = (20.5,-36,8)
FEATURE [Part::Fillet] Fillet
  Base = -> Extrude046
  Edges = 1 edges r=3.9: [Edge12]
FEATURE [Part::Fillet] Fillet048
  Base = -> Fillet
  Edges = 1 edges r=3.9: [Edge8]
FEATURE [Part::Fillet] Fillet049
  Base = -> Fillet048
  Edges = 1 edges r=3.9: [Edge17]
FEATURE [Part::Fillet] Fillet050
  Base = -> Fillet049
  Edges = 1 edges r=3.9: [Edge11]
  Placement = pos=(-55,0,8.3) rot=(1,0,0;0.191986rad)
FEATURE [Part::MultiFuse] Fusion049
  Shapes = -> [Fillet031,Fillet036,Fillet037]
FEATURE [Part::Cut] Cut027
  Base = -> Cylinder005
  Placement = pos=(0,0,-30) rot=(0,0,1;0rad)
  Tool = -> Box081
FEATURE [Sketcher::SketchObject] Sketch049
  FullyConstrained = true
  sketch-geometry (4):
    g0: LineSegment StartX=-5.1 StartY=-34.18 StartZ=0 EndX=5.1 EndY=-34.18 EndZ=0
    g1: LineSegment StartX=-5.1 StartY=-3.93167e-07 StartZ=0 EndX=-5.1 EndY=-34.18 EndZ=0
    g2: LineSegment StartX=5.1 StartY=-34.18 StartZ=0 EndX=5.1 EndY=-3.93167e-07 EndZ=0
    g3: LineSegment StartX=-5.1 StartY=-3.93167e-07 StartZ=0 EndX=5.1 EndY=-3.93167e-07 EndZ=0
  constraints (10):
    c: Horizontal(g0)
    c: Block(g0)
    c: Coincident(g1,g0)
    c: Vertical(g1)
    c: Coincident(g2,g0)
    c: Vertical(g2)
    c: Coincident(g3,g1)
    c: Coincident(g3,g2)
    c: Horizontal(g3)
    c: Block(g3)
FEATURE [Part::Extrusion] Extrude047
  Base = -> Sketch049
  Dir = (0,0,1)
  DirMode = 2
  FaceMakerClass = Part::FaceMakerBullseye
  LengthFwd = 6.2
  LengthRev = 0
  Solid = true
  Symmetric = false
FEATURE [Part::Fillet] Fillet054
  Base = -> Extrude047
  Edges = 1 edges r=3.09: [Edge7]
FEATURE [Part::Fillet] Fillet051
  Base = -> Fillet054
  Edges = 1 edges r=3.09: [Edge8]
FEATURE [Part::Fillet] Fillet052
  Base = -> Fillet051
  Edges = 1 edges r=3.09: [Edge17]
FEATURE [Part::Fillet] Fillet053  label="removeFromMainToMakeUSBCableHole001"
  Base = -> Fillet052
  Edges = 1 edges r=3.09: [Edge10]
  Placement = pos=(-111.4,30,14.9) rot=(0,1,0;1.5708rad)
FEATURE [Sketcher::SketchObject] Sketch050
  FullyConstrained = true
  sketch-geometry (4):
    g0: LineSegment StartX=-5.1 StartY=-34.18 StartZ=0 EndX=5.1 EndY=-34.18 EndZ=0
    g1: LineSegment StartX=-5.1 StartY=-3.93167e-07 StartZ=0 EndX=-5.1 EndY=-34.18 EndZ=0
    g2: LineSegment StartX=5.1 StartY=-34.18 StartZ=0 EndX=5.1 EndY=-3.93167e-07 EndZ=0
    g3: LineSegment StartX=-5.1 StartY=-3.93167e-07 StartZ=0 EndX=5.1 EndY=-3.93167e-07 EndZ=0
  constraints (10):
    c: Horizontal(g0)
    c: Block(g0)
    c: Coincident(g1,g0)
    c: Vertical(g1)
    c: Coincident(g2,g0)
    c: Vertical(g2)
    c: Coincident(g3,g1)
    c: Coincident(g3,g2)
    c: Horizontal(g3)
    c: Block(g3)
FEATURE [Part::Extrusion] Extrude048
  Base = -> Sketch050
  Dir = (0,0,1)
  DirMode = 2
  FaceMakerClass = Part::FaceMakerBullseye
  LengthFwd = 6.2
  LengthRev = 0
  Solid = true
  Symmetric = false
FEATURE [Part::Fillet] Fillet058
  Base = -> Extrude048
  Edges = 1 edges r=3.09: [Edge7]
FEATURE [Part::Fillet] Fillet056
  Base = -> Fillet058
  Edges = 1 edges r=3.09: [Edge8]
FEATURE [Part::Fillet] Fillet055
  Base = -> Fillet056
  Edges = 1 edges r=3.09: [Edge17]
FEATURE [Part::Fillet] Fillet057  label="removeFromMainToMakeUSBCableHole002"
  Base = -> Fillet055
  Edges = 1 edges r=3.09: [Edge10]
  Placement = pos=(-111.4,30,18.4) rot=(0,1,0;1.5708rad)
FEATURE [Part::MultiFuse] Fusion050  label="removeFusion050"
  Shapes = -> [Fillet057,Fillet053,Fillet042]
FEATURE [Part::Box] Box082  label="Cube082"
  AttacherType = Attacher::AttachEngine3D
  Height = 3
  Length = 3
  Placement = pos=(-20,-23.5,17) rot=(0,0,1;0rad)
  Width = 23
FEATURE [Part::Box] Box083  label="Cube083"
  AttacherType = Attacher::AttachEngine3D
  Height = 3
  Length = 3
  Placement = pos=(-40,-23.5,17) rot=(0,0,1;0rad)
  Width = 23
FEATURE [Part::Box] Box086  label="Cube086"
  AttacherType = Attacher::AttachEngine3D
  Height = 8
  Length = 28
  Placement = pos=(-132,-26,0) rot=(0,0,1;0rad)
  Width = 23
FEATURE [Part::Box] Box087  label="Cube087"
  AttacherType = Attacher::AttachEngine3D
  Height = 8
  Length = 12
  Placement = pos=(-98,-26,0) rot=(0,0,1;0rad)
  Width = 23
FEATURE [Part::Box] Box088  label="Cube088"
  AttacherType = Attacher::AttachEngine3D
  Height = 8
  Length = 12
  Placement = pos=(-108,-10,0) rot=(0,0,1;0rad)
  Width = 8
FEATURE [Part::MultiFuse] Fusion051  label="extraStrengthFusion051"
  Shapes = -> [Box087,Box088,Box086]
FEATURE [Part::Fillet] Fillet059
  Base = -> Fusion051
  Edges = 1 edges r=4: [Edge8]
FEATURE [Part::MultiFuse] Fusion052  label="main"
  Shapes = -> [Box083,Box082,Cut017,Extrude001,Fillet059,Revolve]
FEATURE [Part::Cut] Cut028
  Base = -> Fusion052
  Tool = -> Fusion050
FEATURE [Part::Fillet] Fillet060
  Base = -> Cut028
  Edges = 1 edges r=2: [Edge287]
FEATURE [Part::Cut] Cut029
  Base = -> Fillet060
  Tool = -> Fillet050
FEATURE [Part::Cut] Cut030
  Base = -> Cut029
  Tool = -> Fusion049
FEATURE [Part::Cut] Cut031
  Base = -> Cut030
  Tool = -> Fusion037
